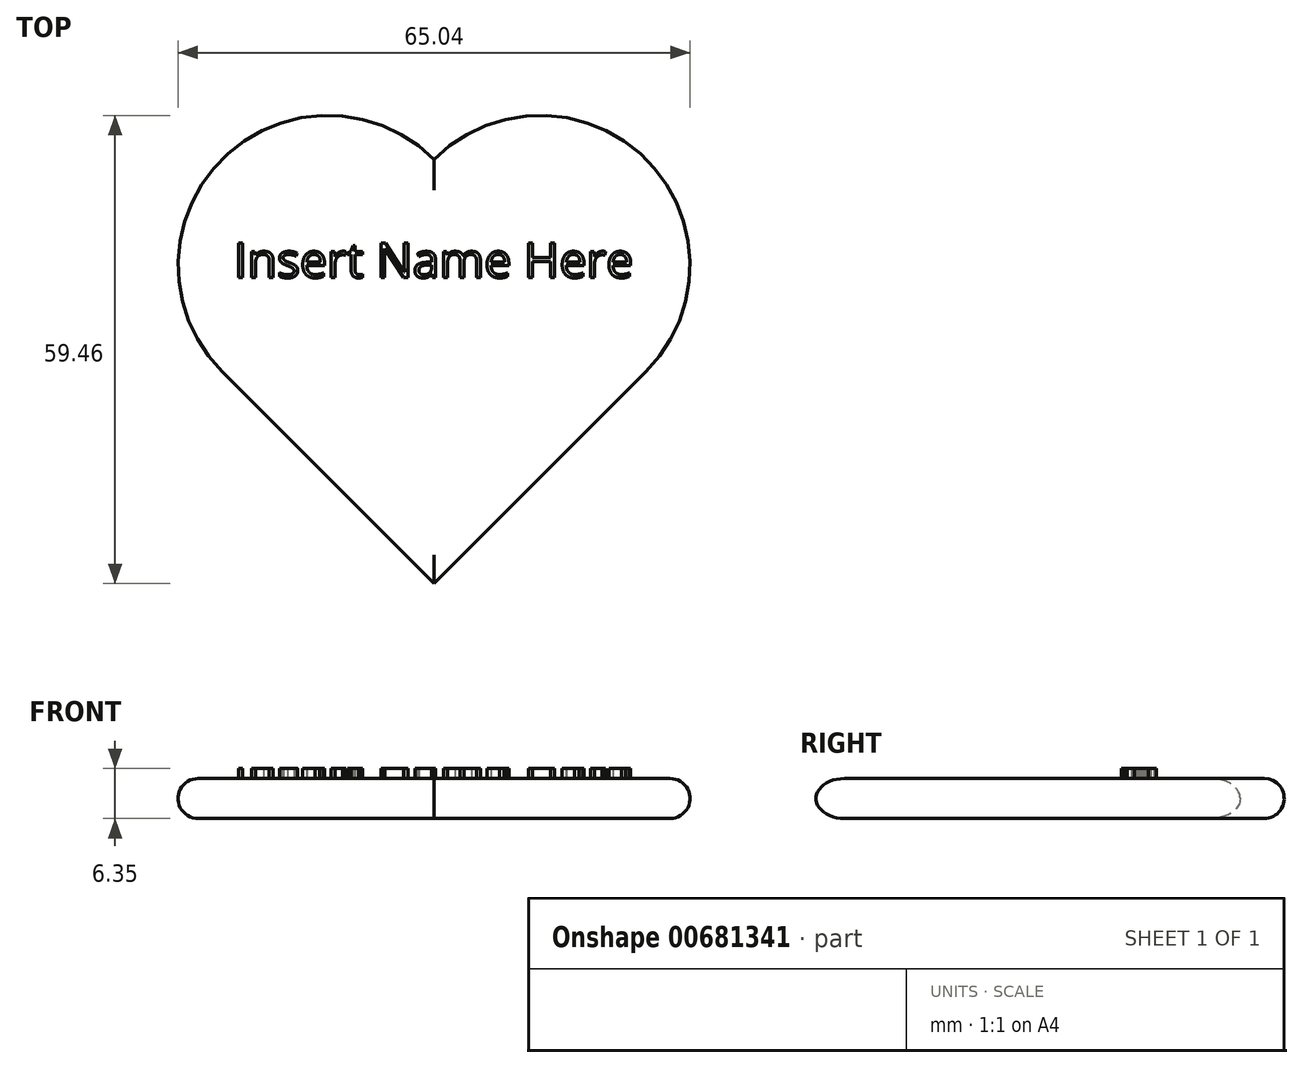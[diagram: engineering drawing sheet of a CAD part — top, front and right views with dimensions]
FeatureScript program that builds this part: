
annotation { "Feature Type Name" : "Feature", "Feature Type Description" : "" }
export const myFeature = defineFeature(function(context is Context, id is Id, definition is map)
    precondition{}
    {
        {
            var Q0;
            Q0=qCreatedBy(makeId("Top.planeOp"),FACE);
            var sketch = newSketch(context, id + "F0", { "sketchPlane" : qUnion([Q0])});
            skLineSegment(sketch, "E0", {"start": v(-40.54, 22.68) * mm, "end": v(-40.54, -15.42) * mm});
            skLineSegment(sketch, "E1", {"start": v(-40.54, -15.42) * mm, "end": v(-2.44, -15.42) * mm});
            skArc(sketch, "E2", {"start": v(-2.44, 22.68) * mm, "mid": v(-21.49, 41.73) * mm, "end": v(-40.54, 22.68) * mm});
            skArc(sketch, "E3", {"start": v(-2.44, -15.42) * mm, "mid": v(16.61, 3.63) * mm, "end": v(-2.44, 22.68) * mm});
            skPoint(sketch, "E4.endSnap0", {"position": v(-21.49, 41.73) * mm});
            skPoint(sketch, "E5.endSnap0", {"position": v(16.61, 3.63) * mm});
            skSolve(sketch);
        }
        {
            var Q0;
            Q0=makeQuery(id+"F0.imprint","IMPRINT",FACE,{"disambiguationData":[TD([[makeQuery(id+"F0.imprint","IMPRINT",EDGE,{"derivedFrom":sQuery(id+"F0.wireOp",EDGE,"E0")}),1.0]])]});
            extrude(context, id + "F1", {"entities" : qUnion([Q0]), "depth" : 5.08 * mm, "offsetDistance" : 25.4 * mm});
        }
        {
            var Q0;
            Q0=makeQuery(id+"F1.opExtrude","SWEPT_BODY",BODY,{"disambiguationData":[OSD([sQuery(id+"F0.wireOp",EDGE,"E0"),sQuery(id+"F0.wireOp",EDGE,"E1"),sQuery(id+"F0.wireOp",EDGE,"E2"),sQuery(id+"F0.wireOp",EDGE,"E3")])]});
            var Q1;
            Q1=makeQuery(id+"F1.opExtrude","SWEPT_EDGE",EDGE,{"disambiguationData":[OSD([sQuery(id+"F0.wireOp",EDGE,"E0"),sQuery(id+"F0.wireOp",EDGE,"E1")])]});
            transform(context, id + "F2", {"entities" : qUnion([Q0]), "transformType" : TransformType.ROTATION, "transformAxis" : qUnion([Q1]), "angle" : 315 * degree, "makeCopy" : false});
        }
        {
            var Q0;
            Q0=makeQuery(id+"F1.opExtrude","CAP_FACE",FACE,{"disambiguationData":[OSD([sQuery(id+"F0.wireOp",EDGE,"E0"),sQuery(id+"F0.wireOp",EDGE,"E1"),sQuery(id+"F0.wireOp",EDGE,"E2"),sQuery(id+"F0.wireOp",EDGE,"E3")])],"isStart":false});
            var sketch = newSketch(context, id + "F3", { "sketchPlane" : qUnion([Q0])});
            skText(sketch, "E6", { "text": "Insert Name Here", "fontName": "OpenSans-Regular.ttf"});
            const initialGuessF3  = {"E6": [-0.06596, 0.02345, 1, 0, 0.00441]};
            skSetInitialGuess(sketch, initialGuessF3);
            skSolve(sketch);
        }
        {
            var Q0;
            Q0=qSketchRegion(id+"F3",true);
            extrude(context, id + "F4", {"entities" : qUnion([Q0]), "operationType" : NewBodyOperationType.ADD, "depth" : 1.27 * mm, "offsetDistance" : 25.4 * mm});
        }
        {
            var Q0;
            Q0=makeQuery(id+"F1.opExtrude","CAP_EDGE",EDGE,{"disambiguationData":[OSD([sQuery(id+"F0.wireOp",EDGE,"E1")])],"isStart":false});
            var Q1;
            Q1=makeQuery(id+"F1.opExtrude","CAP_EDGE",EDGE,{"disambiguationData":[OSD([sQuery(id+"F0.wireOp",EDGE,"E0")])],"isStart":false});
            var Q2;
            Q2=makeQuery(id+"F1.opExtrude","CAP_FACE",FACE,{"disambiguationData":[OSD([sQuery(id+"F0.wireOp",EDGE,"E0"),sQuery(id+"F0.wireOp",EDGE,"E1"),sQuery(id+"F0.wireOp",EDGE,"E2"),sQuery(id+"F0.wireOp",EDGE,"E3")])],"isStart":true});
            fillet(context, id + "F5", {"entities" : qUnion([Q0, Q1, Q2]), "radius" : 2.54 * mm, "tangentPropagation" : true, "allowEdgeOverflow" : false});
        }
    });
